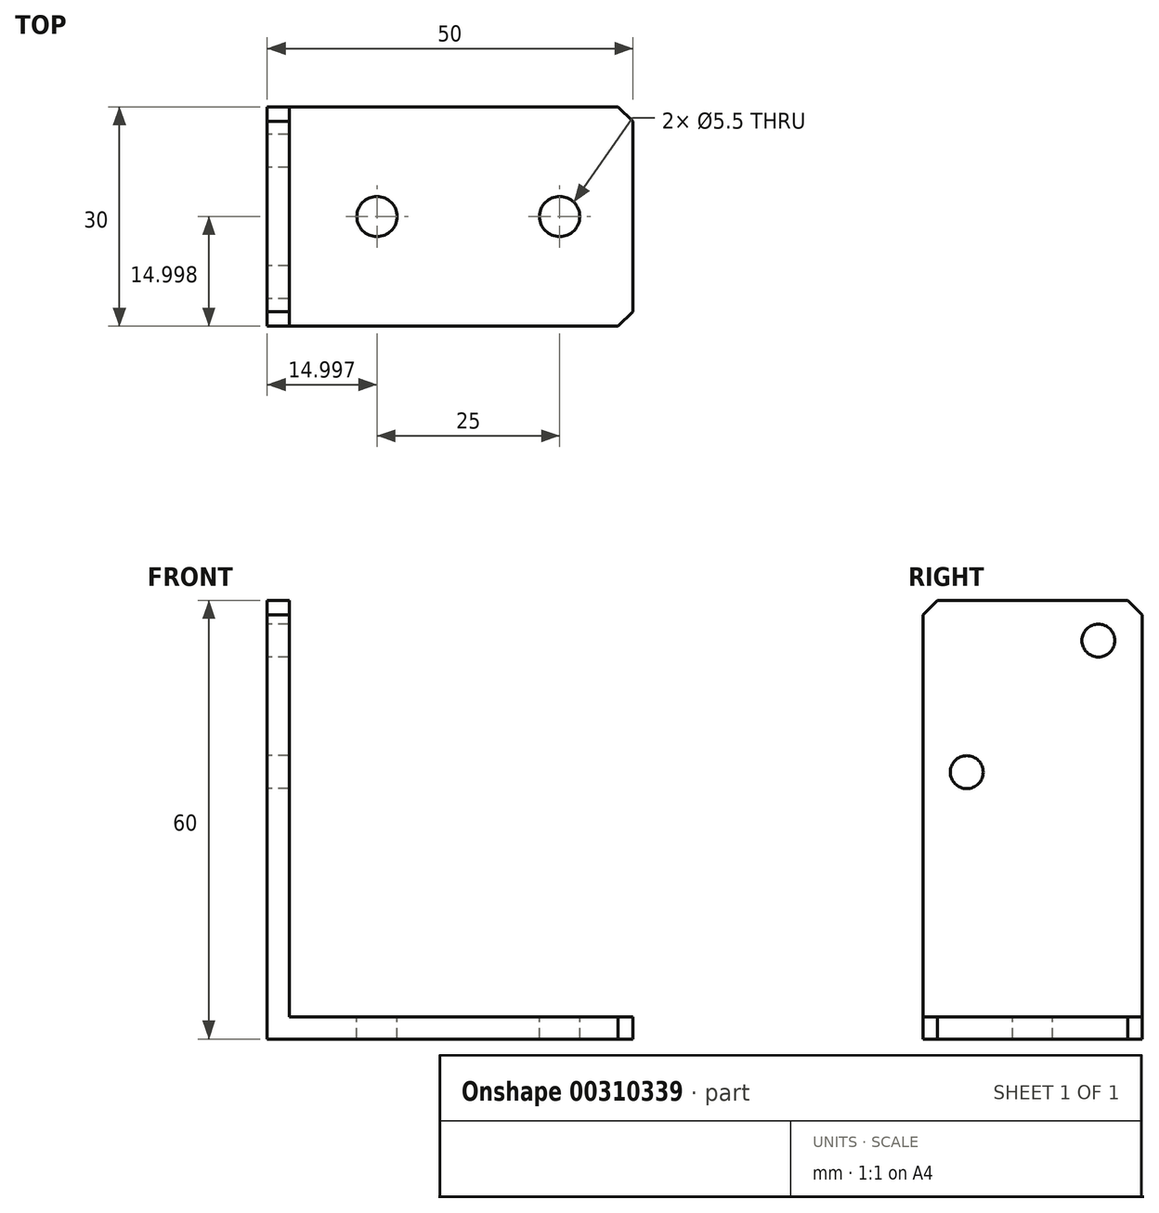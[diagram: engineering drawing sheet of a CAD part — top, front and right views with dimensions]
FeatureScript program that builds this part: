
annotation { "Feature Type Name" : "Feature", "Feature Type Description" : "" }
export const myFeature = defineFeature(function(context is Context, id is Id, definition is map)
    precondition{}
    {
        {
            var Q0;
            Q0=qCreatedBy(makeId("Top.planeOp"),FACE);
            var sketch = newSketch(context, id + "F0", { "sketchPlane" : qUnion([Q0])});
            skLineSegment(sketch, "E0.bottom", {"start": v(-25.1, 0.19) * mm, "end": v(24.9, 0.19) * mm});
            skLineSegment(sketch, "E0.top", {"start": v(-25.1, -29.81) * mm, "end": v(24.9, -29.81) * mm});
            skLineSegment(sketch, "E0.left", {"start": v(-25.1, 0.19) * mm, "end": v(-25.1, -29.81) * mm});
            skLineSegment(sketch, "E0.right", {"start": v(24.9, 0.19) * mm, "end": v(24.9, -29.81) * mm});
            skLineSegment(sketch, "E1.0", {"start": v(-22.1, 0.19) * mm, "end": v(-22.1, -29.81) * mm});
            skSolve(sketch);
        }
        {
            var Q0;
            {var subQ0=sQuery(id+"F0.wireOp",EDGE,"E0.right");Q0=makeQuery(id+"F0.imprint","IMPRINT",FACE,{"disambiguationData":[TD([[makeQuery(id+"F0.imprint","IMPRINT",EDGE,{"derivedFrom":subQ0}),-1.0]])]});}
            extrude(context, id + "F1", {"entities" : qUnion([Q0]), "depth" : 3 * mm});
        }
        {
            var Q0;
            {var subQ0=sQuery(id+"F0.wireOp",EDGE,"E0.left");Q0=makeQuery(id+"F0.imprint","IMPRINT",FACE,{"disambiguationData":[TD([[makeQuery(id+"F0.imprint","IMPRINT",EDGE,{"derivedFrom":subQ0}),1.0]])]});}
            extrude(context, id + "F2", {"entities" : qUnion([Q0]), "operationType" : NewBodyOperationType.ADD, "depth" : 60 * mm});
        }
        {
            var Q0;
            Q0=makeQuery(id+"F2.opExtrude","SWEPT_FACE",FACE,{"disambiguationData":[OSD([sQuery(id+"F0.wireOp",EDGE,"E0.left")])]});
            var sketch = newSketch(context, id + "F3", { "sketchPlane" : qUnion([Q0])});
            skLineSegment(sketch, "E2.bottom", {"start": v(-0.19, 60) * mm, "end": v(29.81, 60) * mm});
            skLineSegment(sketch, "E2.top", {"start": v(-0.19, 0) * mm, "end": v(29.81, 0) * mm});
            skLineSegment(sketch, "E2.left", {"start": v(-0.19, 60) * mm, "end": v(-0.19, 0) * mm});
            skLineSegment(sketch, "E2.right", {"start": v(29.81, 60) * mm, "end": v(29.81, 0) * mm});
            skLineSegment(sketch, "E3.0", {"start": v(-0.19, 54.5) * mm, "end": v(29.81, 54.5) * mm});
            skLineSegment(sketch, "E4.0", {"start": v(23.81, 60) * mm, "end": v(23.81, 0) * mm});
            skLineSegment(sketch, "E5.0", {"start": v(5.81, 60) * mm, "end": v(5.81, 0) * mm});
            skPoint(sketch, "E6", {"position": v(5.81, 54.5) * mm});
            skPoint(sketch, "E7", {"position": v(23.81, 54.5) * mm});
            skLineSegment(sketch, "E8.0", {"start": v(-0.19, 36.5) * mm, "end": v(29.81, 36.5) * mm});
            skPoint(sketch, "E9", {"position": v(5.81, 36.5) * mm});
            skPoint(sketch, "E10", {"position": v(23.81, 36.5) * mm});
            skSolve(sketch);
        }
        {
            var Q0;
            Q0=sQuery(id+"F3.wireOp",VERTEX,"E6");
            var Q1;
            Q1=sQuery(id+"F3.wireOp",VERTEX,"E10");
            var Q2;
            Q2=makeQuery(id+"F1.opExtrude","SWEPT_BODY",BODY,{"disambiguationData":[OSD([sQuery(id+"F0.wireOp",EDGE,"E0.bottom"),sQuery(id+"F0.wireOp",EDGE,"E0.top"),sQuery(id+"F0.wireOp",EDGE,"E0.right"),sQuery(id+"F0.wireOp",EDGE,"E1.0")])]});
            hole(context, id + "F4", {"style" : HoleStyle.SIMPLE, "endStyle" : HoleEndStyle.BLIND, "holeDiameter" : 4.5 * mm, "holeDepth" : 12.4 * mm, "tappedDepth" : 10 * mm, "tapClearance" : 3, "startFromSketch" : true, "locations" : qUnion([Q0, Q1]), "scope" : qUnion([Q2])});
        }
        {
            var Q0;
            Q0=makeQuery(id+"F1.opExtrude","CAP_FACE",FACE,{"disambiguationData":[OSD([sQuery(id+"F0.wireOp",EDGE,"E0.bottom"),sQuery(id+"F0.wireOp",EDGE,"E0.top"),sQuery(id+"F0.wireOp",EDGE,"E0.right"),sQuery(id+"F0.wireOp",EDGE,"E1.0")])],"isStart":false});
            var sketch = newSketch(context, id + "F5", { "sketchPlane" : qUnion([Q0])});
            skLineSegment(sketch, "E11.bottom", {"start": v(-22.1, 0.19) * mm, "end": v(24.9, 0.19) * mm});
            skLineSegment(sketch, "E11.top", {"start": v(-22.1, -29.81) * mm, "end": v(24.9, -29.81) * mm});
            skLineSegment(sketch, "E11.left", {"start": v(-22.1, 0.19) * mm, "end": v(-22.1, -29.81) * mm});
            skLineSegment(sketch, "E11.right", {"start": v(24.9, 0.19) * mm, "end": v(24.9, -29.81) * mm});
            skLineSegment(sketch, "E12.0", {"start": v(-22.1, -14.81) * mm, "end": v(24.9, -14.81) * mm});
            skLineSegment(sketch, "E13.0", {"start": v(14.9, 0.19) * mm, "end": v(14.9, -29.81) * mm});
            skLineSegment(sketch, "E14.0", {"start": v(-10.1, 0.19) * mm, "end": v(-10.1, -29.81) * mm});
            skPoint(sketch, "E15", {"position": v(-10.1, -14.81) * mm});
            skPoint(sketch, "E16", {"position": v(14.9, -14.81) * mm});
            skSolve(sketch);
        }
        {
            var Q0;
            Q0=sQuery(id+"F5.wireOp",VERTEX,"E15");
            var Q1;
            Q1=sQuery(id+"F5.wireOp",VERTEX,"E16");
            var Q2;
            Q2=makeQuery(id+"F1.opExtrude","SWEPT_BODY",BODY,{"disambiguationData":[OSD([sQuery(id+"F0.wireOp",EDGE,"E0.bottom"),sQuery(id+"F0.wireOp",EDGE,"E0.top"),sQuery(id+"F0.wireOp",EDGE,"E0.right"),sQuery(id+"F0.wireOp",EDGE,"E1.0")])]});
            hole(context, id + "F6", {"style" : HoleStyle.SIMPLE, "endStyle" : HoleEndStyle.BLIND, "holeDiameter" : 5.5 * mm, "holeDepth" : 12.4 * mm, "tappedDepth" : 10 * mm, "tapClearance" : 3, "startFromSketch" : true, "locations" : qUnion([Q0, Q1]), "scope" : qUnion([Q2])});
        }
        {
            var Q0;
            Q0=makeQuery(id+"F2.opExtrude","CAP_EDGE",EDGE,{"disambiguationData":[OSD([sQuery(id+"F0.wireOp",EDGE,"E0.top")])],"isStart":false});
            var Q1;
            Q1=makeQuery(id+"F2.opExtrude","CAP_EDGE",EDGE,{"disambiguationData":[OSD([sQuery(id+"F0.wireOp",EDGE,"E0.bottom")])],"isStart":false});
            var Q2;
            Q2=makeQuery(id+"F1.opExtrude","SWEPT_EDGE",EDGE,{"disambiguationData":[OSD([sQuery(id+"F0.wireOp",EDGE,"E0.top"),sQuery(id+"F0.wireOp",EDGE,"E0.right")])]});
            var Q3;
            Q3=makeQuery(id+"F1.opExtrude","SWEPT_EDGE",EDGE,{"disambiguationData":[OSD([sQuery(id+"F0.wireOp",EDGE,"E0.bottom"),sQuery(id+"F0.wireOp",EDGE,"E0.right")])]});
            chamfer(context, id + "F7", {"entities" : qUnion([Q0, Q1, Q2, Q3]), "width" : 2 * mm, "tangentPropagation" : true});
        }
    });
